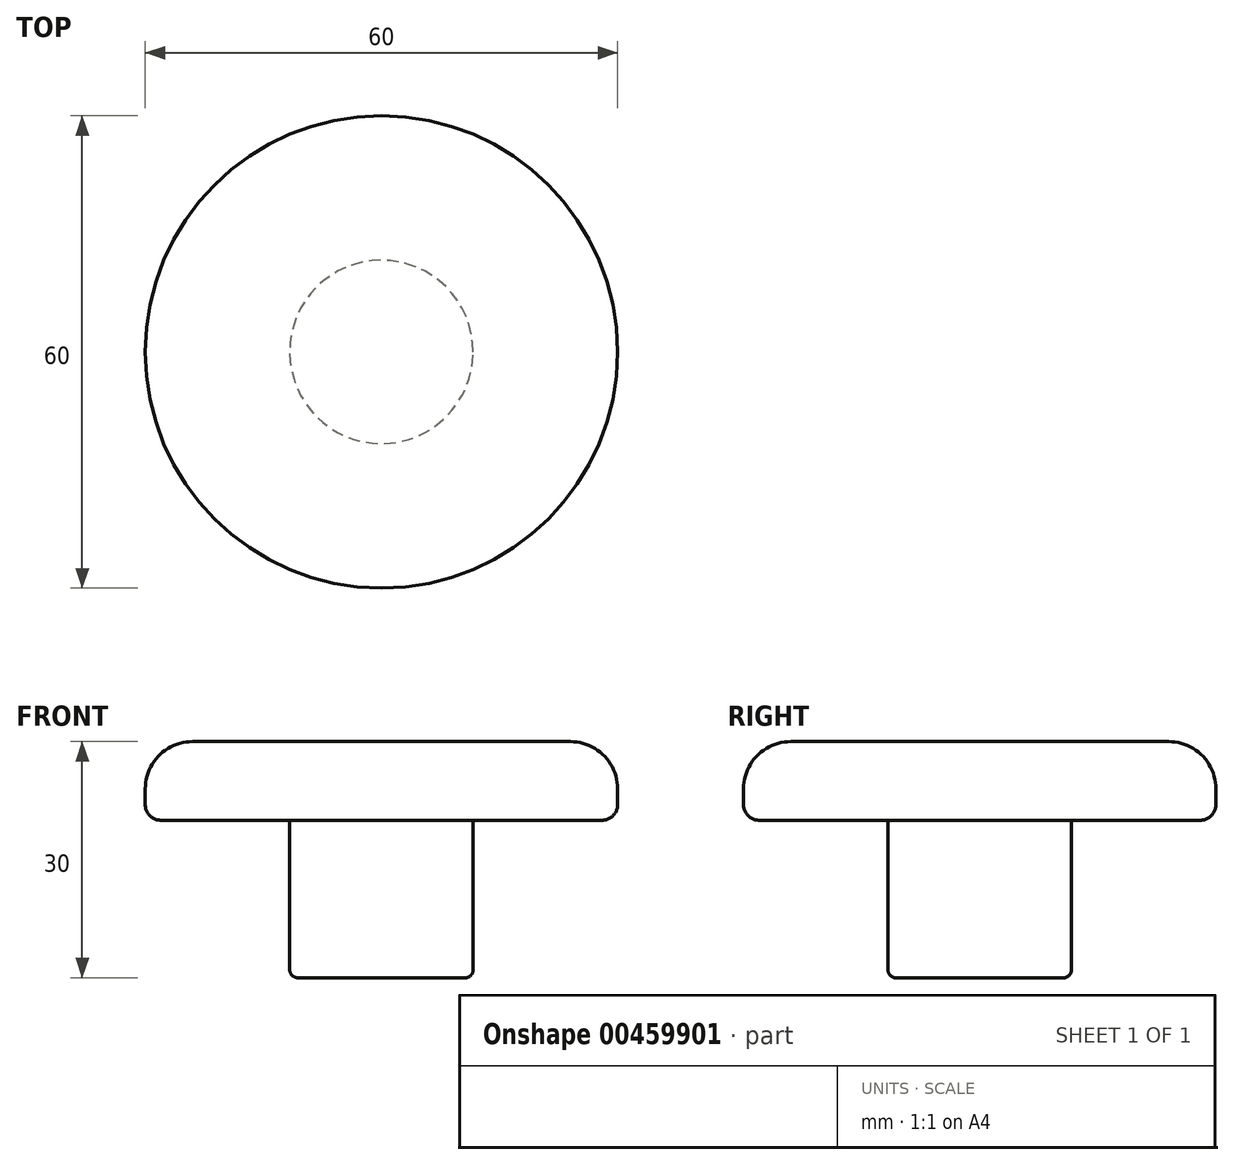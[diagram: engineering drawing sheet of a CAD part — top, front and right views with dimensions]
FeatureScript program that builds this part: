
annotation { "Feature Type Name" : "Feature", "Feature Type Description" : "" }
export const myFeature = defineFeature(function(context is Context, id is Id, definition is map)
    precondition{}
    {
        {
            var Q0;
            Q0=qCreatedBy(makeId("Right.planeOp"),FACE);
            var sketch = newSketch(context, id + "F0", { "sketchPlane" : qUnion([Q0])});
            skLineSegment(sketch, "E0", {"start": v(0, 0) * mm, "end": v(0, 30) * mm});
            skLineSegment(sketch, "E1", {"start": v(0, 30) * mm, "end": v(24, 30) * mm});
            skLineSegment(sketch, "E2", {"start": v(30, 24) * mm, "end": v(30, 22) * mm});
            skLineSegment(sketch, "E3", {"start": v(28, 20) * mm, "end": v(11.65, 20) * mm});
            skLineSegment(sketch, "E4", {"start": v(11.65, 20) * mm, "end": v(11.65, 1) * mm});
            skLineSegment(sketch, "E5", {"start": v(10.65, 0) * mm, "end": v(0, 0) * mm});
            skPoint(sketch, "E6.visualSharp", {"position": v(30, 30) * mm});
            skArc(sketch, "E6.filletArc", {"start": v(30, 24) * mm, "mid": v(28.24, 28.24) * mm, "end": v(24, 30) * mm});
            skPoint(sketch, "E7.visualSharp", {"position": v(30, 20) * mm});
            skArc(sketch, "E7.filletArc", {"start": v(28, 20) * mm, "mid": v(29.41, 20.59) * mm, "end": v(30, 22) * mm});
            skPoint(sketch, "E8.visualSharp", {"position": v(11.65, 0) * mm});
            skArc(sketch, "E8.filletArc", {"start": v(10.65, 0) * mm, "mid": v(11.36, 0.3) * mm, "end": v(11.65, 1) * mm});
            skSolve(sketch);
        }
        {
            var Q0;
            Q0 = qSketchRegion(id + "F0", true);
            var Q1;
            Q1=sQuery(id+"F0.wireOp",EDGE,"E0");
            revolve(context, id + "F1", {"entities" : qUnion([Q0]), "axis" : qUnion([Q1]), "revolveType" : RevolveType.FULL});
        }
    });
